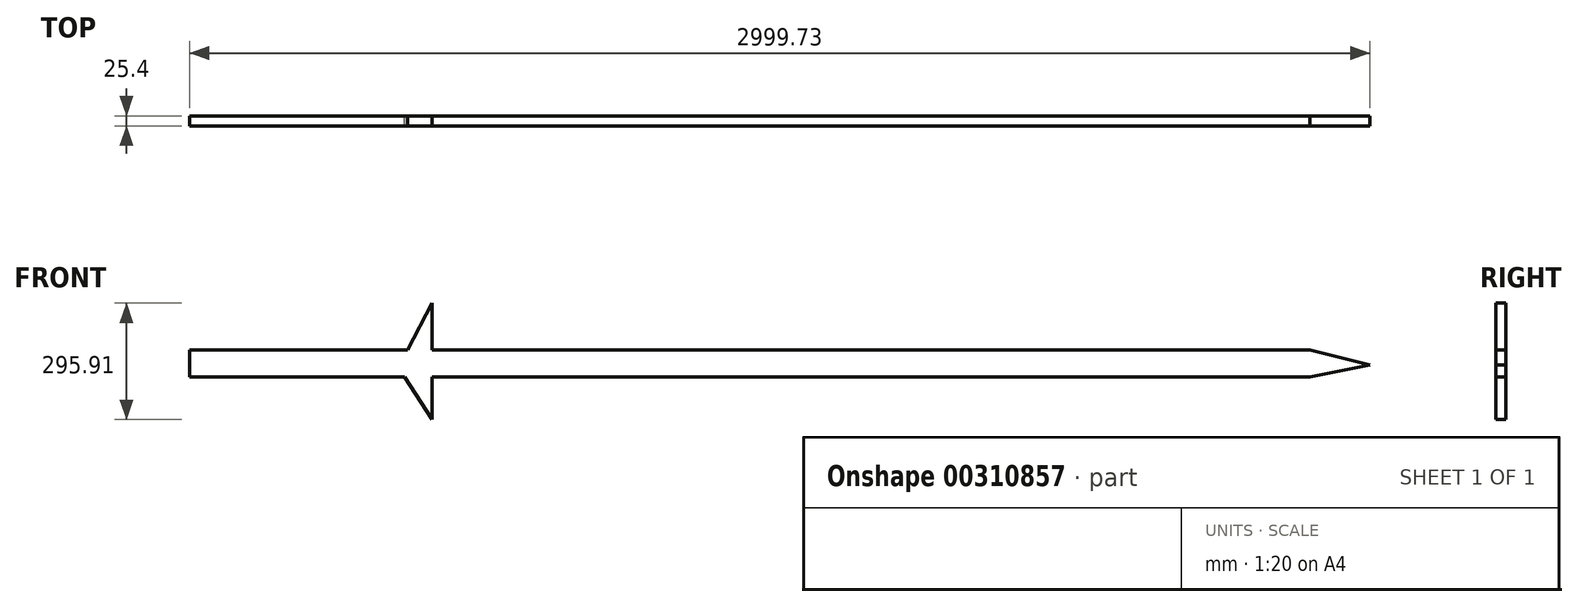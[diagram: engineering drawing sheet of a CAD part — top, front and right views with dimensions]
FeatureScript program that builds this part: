
annotation { "Feature Type Name" : "Feature", "Feature Type Description" : "" }
export const myFeature = defineFeature(function(context is Context, id is Id, definition is map)
    precondition{}
    {
        {
            var Q0;
            Q0=qCreatedBy(makeId("Front.planeOp"),FACE);
            var sketch = newSketch(context, id + "F0", { "sketchPlane" : qUnion([Q0])});
            skLineSegment(sketch, "E0", {"start": v(0, 0) * mm, "end": v(616.1, 0) * mm});
            skLineSegment(sketch, "E1", {"start": v(616.1, 0) * mm, "end": v(616.1, 68.6) * mm});
            skLineSegment(sketch, "E2", {"start": v(616.1, 68.6) * mm, "end": v(0, 68.6) * mm});
            skLineSegment(sketch, "E3", {"start": v(0, 68.6) * mm, "end": v(0, 0) * mm});
            skLineSegment(sketch, "E4", {"start": v(616.1, 68.6) * mm, "end": v(616.1, 187.74) * mm});
            skLineSegment(sketch, "E5", {"start": v(616.1, 187.74) * mm, "end": v(554.63, 68.6) * mm});
            skLineSegment(sketch, "E6", {"start": v(554.63, 68.6) * mm, "end": v(616.1, 0) * mm});
            skLineSegment(sketch, "E7", {"start": v(616.1, 0) * mm, "end": v(616.1, -108.17) * mm});
            skLineSegment(sketch, "E8", {"start": v(616.1, -108.17) * mm, "end": v(546.94, 0) * mm});
            skLineSegment(sketch, "E9", {"start": v(546.94, 0) * mm, "end": v(554.63, 68.6) * mm});
            skLineSegment(sketch, "E10", {"start": v(616.1, 68.6) * mm, "end": v(546.94, 0) * mm});
            skLineSegment(sketch, "E11", {"start": v(554.63, 68.6) * mm, "end": v(443.2, 0) * mm});
            skLineSegment(sketch, "E12", {"start": v(443.2, 0) * mm, "end": v(370.18, 68.6) * mm});
            skLineSegment(sketch, "E13", {"start": v(370.18, 68.6) * mm, "end": v(305.71, 0) * mm});
            skLineSegment(sketch, "E14", {"start": v(305.71, 0) * mm, "end": v(193.42, 68.6) * mm});
            skLineSegment(sketch, "E15", {"start": v(193.42, 68.6) * mm, "end": v(116.87, 0) * mm});
            skLineSegment(sketch, "E16", {"start": v(116.87, 0) * mm, "end": v(55.39, 68.6) * mm});
            skLineSegment(sketch, "E17", {"start": v(55.39, 68.6) * mm, "end": v(0, 0) * mm});
            skLineSegment(sketch, "E18", {"start": v(0, 68.6) * mm, "end": v(61.48, 0) * mm});
            skLineSegment(sketch, "E19", {"start": v(61.48, 0) * mm, "end": v(138.04, 68.6) * mm});
            skLineSegment(sketch, "E20", {"start": v(138.04, 68.6) * mm, "end": v(199.52, 0) * mm});
            skLineSegment(sketch, "E21", {"start": v(199.52, 0) * mm, "end": v(276.07, 68.6) * mm});
            skLineSegment(sketch, "E22", {"start": v(276.07, 68.6) * mm, "end": v(378.63, 0) * mm});
            skLineSegment(sketch, "E23", {"start": v(378.63, 0) * mm, "end": v(455.19, 68.6) * mm});
            skLineSegment(sketch, "E24", {"start": v(455.19, 68.6) * mm, "end": v(546.94, 0) * mm});
            skLineSegment(sketch, "E25", {"start": v(616.1, 68.6) * mm, "end": v(2846.65, 68.6) * mm});
            skLineSegment(sketch, "E26", {"start": v(2846.65, 0) * mm, "end": v(2999.73, 30.5) * mm});
            skLineSegment(sketch, "E27", {"start": v(2999.73, 30.5) * mm, "end": v(2846.65, 68.6) * mm});
            skLineSegment(sketch, "E28", {"start": v(616.1, 0) * mm, "end": v(2846.65, 0) * mm});
            skSolve(sketch);
        }
        {
            var Q0;
            Q0 = qSketchRegion(id + "F0", true);
            extrude(context, id + "F1", {"entities" : qUnion([Q0]), "depth" : 25.4 * mm});
        }
    });
